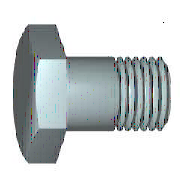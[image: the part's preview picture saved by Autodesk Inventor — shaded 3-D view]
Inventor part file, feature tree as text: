
AUTODESK INVENTOR PART (.ipt)
format: ipt  version: 2021 (Build 250183000, 183)  size: 187,904 bytes
history: native  units: mm (DEFAULTED — no unit token found)
features: sketch x3, extrude x1, chamfer x1, plane x1
ambient origin geometry x7: Origin, YZ Plane, XZ Plane, X Axis, Y Axis, Z Axis, Center Point
bodies: Solid1 (feature_tree), Body (feature_tree)
feature tree (6):
  extrude  "Head"  Depth=110.0mm
  chamfer  "Chamfer1"  Distance=3.5mm
  plane  "Work Plane1"
  sketch  "Sketch1"  dims[d0=110.0mm d1=18.0mm]
  sketch  "Sketch2"  dims[d2=6.0mm]
  sketch  "Sketch4"  dims[d12=90.0deg d3=3.5mm d4=0.0mm d5=30.0deg d21=90.0deg d6=0.61345mm d7=0.61355mm d8=0.0mm d9=0.5001mm d10=8.88mm d11=10.0mm d13=0.61355mm d14=6.0mm d15=18.0mm d16=0.0mm d19=10.0mm d55=45.0deg d57=0.0mm d58=0.0mm]
